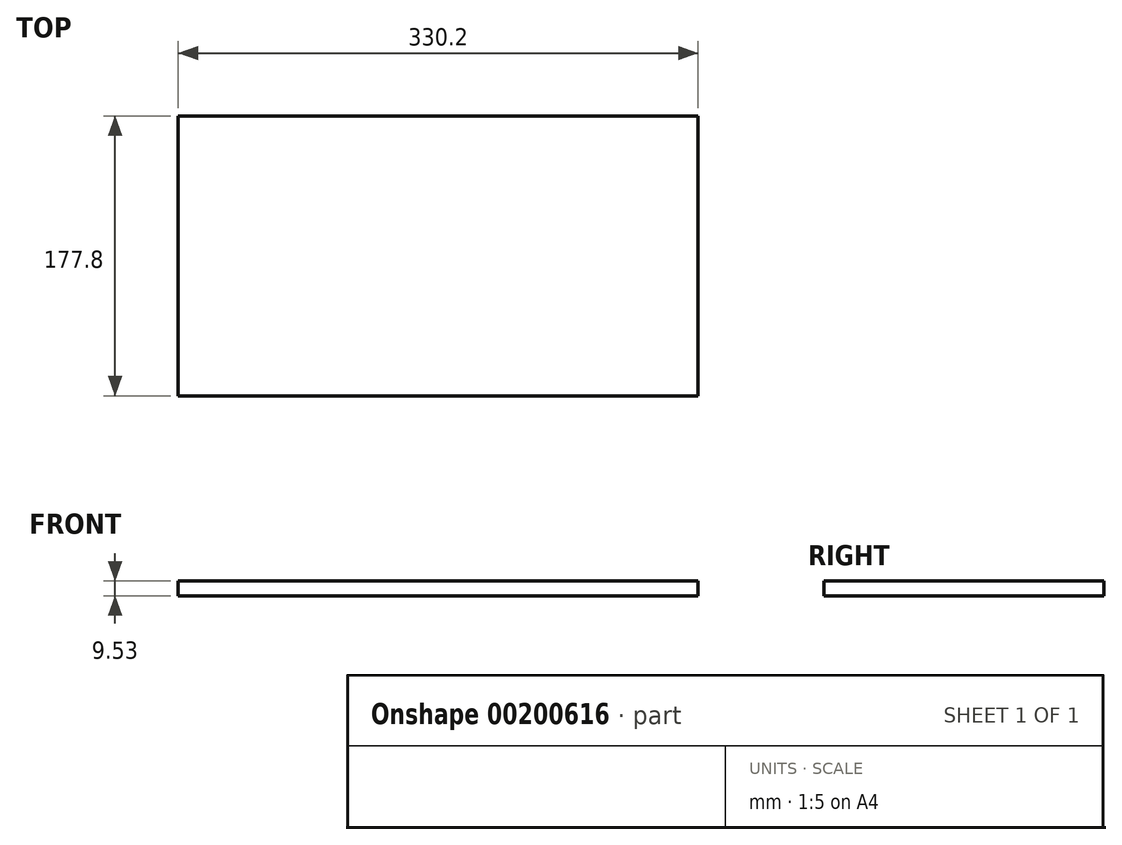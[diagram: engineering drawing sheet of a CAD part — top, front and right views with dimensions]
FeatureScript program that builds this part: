
annotation { "Feature Type Name" : "Feature", "Feature Type Description" : "" }
export const myFeature = defineFeature(function(context is Context, id is Id, definition is map)
    precondition{}
    {
        {
            var Q0;
            Q0=qCreatedBy(makeId("Top.planeOp"),FACE);
            var sketch = newSketch(context, id + "F0", { "sketchPlane" : qUnion([Q0])});
            skLineSegment(sketch, "E0.bottom", {"start": v(165.1, 88.9) * mm, "end": v(-165.1, 88.9) * mm});
            skLineSegment(sketch, "E0.top", {"start": v(165.1, -88.9) * mm, "end": v(-165.1, -88.9) * mm});
            skLineSegment(sketch, "E0.left", {"start": v(165.1, 88.9) * mm, "end": v(165.1, -88.9) * mm});
            skLineSegment(sketch, "E0.right", {"start": v(-165.1, 88.9) * mm, "end": v(-165.1, -88.9) * mm});
            skSolve(sketch);
        }
        {
            var Q0;
            Q0=makeQuery(id+"F0.imprint","IMPRINT",FACE,{"disambiguationData":[TD([[makeQuery(id+"F0.imprint","IMPRINT",EDGE,{"derivedFrom":sQuery(id+"F0.wireOp",EDGE,"E0.bottom")}),1.0]])]});
            extrude(context, id + "F1", {"entities" : qUnion([Q0]), "depth" : 9.52 * mm});
        }
    });
